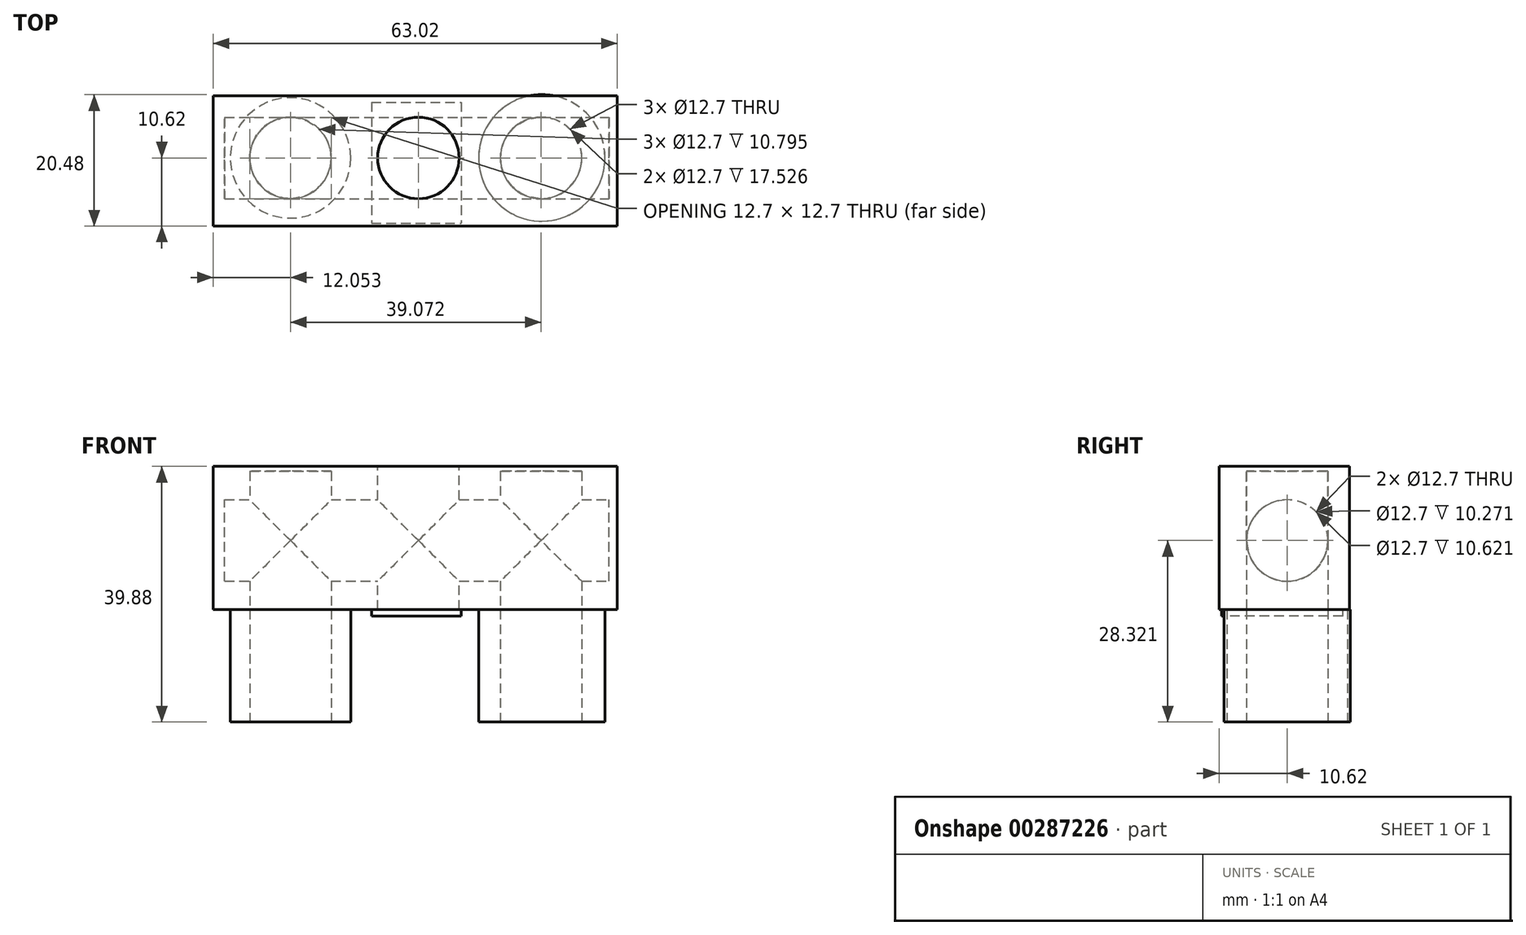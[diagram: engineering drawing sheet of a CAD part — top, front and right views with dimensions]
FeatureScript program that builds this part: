
annotation { "Feature Type Name" : "Feature", "Feature Type Description" : "" }
export const myFeature = defineFeature(function(context is Context, id is Id, definition is map)
    precondition{}
    {
        {
            var Q0;
            Q0=qCreatedBy(makeId("Top.planeOp"),FACE);
            var sketch = newSketch(context, id + "F0", { "sketchPlane" : qUnion([Q0])});
            skCircle(sketch, "E0", {"center": v(-19.95, 0) * mm, "radius": 9.39 * mm});
            skCircle(sketch, "E1", {"center": v(19.24, 0) * mm, "radius": 9.86 * mm});
            skSolve(sketch);
        }
        {
            var Q0;
            Q0 = qSketchRegion(id + "F0", true);
            extrude(context, id + "F1", {"entities" : qUnion([Q0]), "depth" : 17.53 * mm});
        }
        {
            var Q0;
            Q0=makeQuery(id+"F1.opExtrude","CAP_FACE",FACE,{"disambiguationData":[OSD([sQuery(id+"F0.wireOp",EDGE,"E0")])],"isStart":false});
            var sketch = newSketch(context, id + "F2", { "sketchPlane" : qUnion([Q0])});
            skLineSegment(sketch, "E2.bottom", {"start": v(-30.22, 9.68) * mm, "end": v(29.75, 9.68) * mm});
            skLineSegment(sketch, "E2.top", {"start": v(-30.22, -10.62) * mm, "end": v(29.75, -10.62) * mm});
            skLineSegment(sketch, "E2.left", {"start": v(-30.22, 9.68) * mm, "end": v(-30.22, -10.62) * mm});
            skLineSegment(sketch, "E2.right", {"start": v(29.75, 9.68) * mm, "end": v(29.75, -10.62) * mm});
            skSolve(sketch);
        }
        {
            var Q0;
            Q0 = qSketchRegion(id + "F2", true);
            extrude(context, id + "F3", {"entities" : qUnion([Q0]), "depth" : 21.59 * mm});
        }
        {
            var Q0;
            Q0=makeQuery(id+"F3.opExtrude","SWEPT_FACE",FACE,{"disambiguationData":[OSD([sQuery(id+"F2.wireOp",EDGE,"E2.right")])]});
            var sketch = newSketch(context, id + "F4", { "sketchPlane" : qUnion([Q0])});
            skPoint(sketch, "E3", {"position": v(0, 28.32) * mm});
            skPoint(sketch, "E3.positionSnap0", {"position": v(9.68, 28.32) * mm});
            skSolve(sketch);
        }
        {
            var Q0;
            Q0=sQuery(id+"F4.wireOp",VERTEX,"E3");
            var Q1;
            Q1=makeQuery(id+"F3.opExtrude","SWEPT_BODY",BODY,{"disambiguationData":[OSD([sQuery(id+"F2.wireOp",EDGE,"E2.bottom"),sQuery(id+"F2.wireOp",EDGE,"E2.top"),sQuery(id+"F2.wireOp",EDGE,"E2.left"),sQuery(id+"F2.wireOp",EDGE,"E2.right")])]});
            hole(context, id + "F5", {"style" : HoleStyle.SIMPLE, "endStyle" : HoleEndStyle.THROUGH, "holeDiameter" : 12.7 * mm, "tappedDepth" : 12.7 * mm, "tapClearance" : 3, "locations" : qUnion([Q0]), "scope" : qUnion([Q1])});
        }
        {
            var Q0;
            Q0=makeQuery(id+"F1.opExtrude","CAP_FACE",FACE,{"disambiguationData":[OSD([sQuery(id+"F0.wireOp",EDGE,"E0")])],"isStart":true});
            var sketch = newSketch(context, id + "F6", { "sketchPlane" : qUnion([Q0])});
            skPoint(sketch, "E4", {"position": v(-19.95, 0) * mm});
            skPoint(sketch, "E5", {"position": v(19.12, 0) * mm});
            skSolve(sketch);
        }
        {
            var Q0;
            Q0=sQuery(id+"F6.wireOp",VERTEX,"E4");
            var Q1;
            Q1=sQuery(id+"F6.wireOp",VERTEX,"E5");
            var Q2;
            Q2=makeQuery(id+"F3.opExtrude","SWEPT_BODY",BODY,{"disambiguationData":[OSD([sQuery(id+"F2.wireOp",EDGE,"E2.bottom"),sQuery(id+"F2.wireOp",EDGE,"E2.top"),sQuery(id+"F2.wireOp",EDGE,"E2.left"),sQuery(id+"F2.wireOp",EDGE,"E2.right")])]});
            var Q3;
            Q3=makeQuery(id+"F1.opExtrude","SWEPT_BODY",BODY,{"disambiguationData":[OSD([sQuery(id+"F0.wireOp",EDGE,"E0")])]});
            var Q4;
            Q4=makeQuery(id+"F1.opExtrude","SWEPT_BODY",BODY,{"disambiguationData":[OSD([sQuery(id+"F0.wireOp",EDGE,"E1")])]});
            hole(context, id + "F7", {"style" : HoleStyle.SIMPLE, "endStyle" : HoleEndStyle.THROUGH, "holeDiameter" : 12.7 * mm, "tappedDepth" : 12.7 * mm, "tapClearance" : 3, "locations" : qUnion([Q0, Q1]), "scope" : qUnion([Q2, Q3, Q4])});
        }
        {
            var Q0;
            Q0=makeQuery(id+"F3.opExtrude","CAP_FACE",FACE,{"disambiguationData":[OSD([sQuery(id+"F2.wireOp",EDGE,"E2.bottom"),sQuery(id+"F2.wireOp",EDGE,"E2.top"),sQuery(id+"F2.wireOp",EDGE,"E2.left"),sQuery(id+"F2.wireOp",EDGE,"E2.right")])],"isStart":false});
            var sketch = newSketch(context, id + "F8", { "sketchPlane" : qUnion([Q0])});
            skLineSegment(sketch, "E6.bottom", {"start": v(-30.22, -10.62) * mm, "end": v(29.75, -10.62) * mm});
            skLineSegment(sketch, "E6.top", {"start": v(-30.22, 9.68) * mm, "end": v(29.75, 9.68) * mm});
            skLineSegment(sketch, "E6.left", {"start": v(-30.22, -10.62) * mm, "end": v(-30.22, 9.68) * mm});
            skLineSegment(sketch, "E6.right", {"start": v(29.75, -10.62) * mm, "end": v(29.75, 9.68) * mm});
            skSolve(sketch);
        }
        {
            var Q0;
            Q0 = qSketchRegion(id + "F8", true);
            extrude(context, id + "F9", {"entities" : qUnion([Q0]), "operationType" : NewBodyOperationType.ADD, "depth" : 0.76 * mm});
        }
        {
            var Q0;
            Q0=makeQuery(id+"F9.boolean.opBoolean","MERGE",FACE,{"derivedFrom":[makeQuery(id+"F3.opExtrude","SWEPT_FACE",FACE,{"disambiguationData":[OSD([sQuery(id+"F2.wireOp",EDGE,"E2.right")])]}),makeQuery(id+"F9.opExtrude","SWEPT_FACE",FACE,{"disambiguationData":[OSD([sQuery(id+"F8.wireOp",EDGE,"E6.right")])]})]});
            var sketch = newSketch(context, id + "F10", { "sketchPlane" : qUnion([Q0])});
            skLineSegment(sketch, "E7.bottom", {"start": v(-10.62, 17.53) * mm, "end": v(9.68, 17.53) * mm});
            skLineSegment(sketch, "E7.top", {"start": v(-10.62, 39.88) * mm, "end": v(9.68, 39.88) * mm});
            skLineSegment(sketch, "E7.left", {"start": v(-10.62, 17.53) * mm, "end": v(-10.62, 39.88) * mm});
            skLineSegment(sketch, "E7.right", {"start": v(9.68, 17.53) * mm, "end": v(9.68, 39.88) * mm});
            skSolve(sketch);
        }
        {
            var Q0;
            Q0 = qSketchRegion(id + "F10", true);
            extrude(context, id + "F11", {"entities" : qUnion([Q0]), "operationType" : NewBodyOperationType.ADD, "depth" : 1.27 * mm});
        }
        {
            var Q0;
            Q0=makeQuery(id+"F9.boolean.opBoolean","MERGE",FACE,{"derivedFrom":[makeQuery(id+"F3.opExtrude","SWEPT_FACE",FACE,{"disambiguationData":[OSD([sQuery(id+"F2.wireOp",EDGE,"E2.left")])]}),makeQuery(id+"F9.opExtrude","SWEPT_FACE",FACE,{"disambiguationData":[OSD([sQuery(id+"F8.wireOp",EDGE,"E6.left")])]})]});
            var sketch = newSketch(context, id + "F12", { "sketchPlane" : qUnion([Q0])});
            skLineSegment(sketch, "E8.bottom", {"start": v(-9.68, 17.53) * mm, "end": v(10.62, 17.53) * mm});
            skLineSegment(sketch, "E8.top", {"start": v(-9.68, 39.88) * mm, "end": v(10.62, 39.88) * mm});
            skLineSegment(sketch, "E8.left", {"start": v(-9.68, 17.53) * mm, "end": v(-9.68, 39.88) * mm});
            skLineSegment(sketch, "E8.right", {"start": v(10.62, 17.53) * mm, "end": v(10.62, 39.88) * mm});
            skSolve(sketch);
        }
        {
            var Q0;
            Q0=makeQuery(id+"F14.boolean.opBoolean","MERGE",FACE,{"derivedFrom":[makeQuery(id+"F11.boolean.opBoolean","MERGE",FACE,{"derivedFrom":[makeQuery(id+"F9.opExtrude","CAP_FACE",FACE,{"disambiguationData":[OSD([sQuery(id+"F8.wireOp",EDGE,"E6.bottom"),sQuery(id+"F8.wireOp",EDGE,"E6.top"),sQuery(id+"F8.wireOp",EDGE,"E6.left"),sQuery(id+"F8.wireOp",EDGE,"E6.right")])],"isStart":false}),makeQuery(id+"F11.opExtrude","SWEPT_FACE",FACE,{"disambiguationData":[OSD([sQuery(id+"F10.wireOp",EDGE,"E7.top")])]})]}),makeQuery(id+"F14.opExtrude","SWEPT_FACE",FACE,{"disambiguationData":[OSD([sQuery(id+"F12.wireOp",EDGE,"E8.top")])]})]});
            var sketch = newSketch(context, id + "F13", { "sketchPlane" : qUnion([Q0])});
            skPoint(sketch, "E9", {"position": v(0, 0) * mm});
            skSolve(sketch);
        }
        {
            var Q0;
            Q0 = qSketchRegion(id + "F12", true);
            extrude(context, id + "F14", {"entities" : qUnion([Q0]), "operationType" : NewBodyOperationType.ADD, "depth" : 1.78 * mm});
        }
        {
            var Q0;
            Q0=sQuery(id+"F13.wireOp",VERTEX,"E9");
            var Q1;
            Q1=makeQuery(id+"F3.opExtrude","SWEPT_BODY",BODY,{"disambiguationData":[OSD([sQuery(id+"F2.wireOp",EDGE,"E2.bottom"),sQuery(id+"F2.wireOp",EDGE,"E2.top"),sQuery(id+"F2.wireOp",EDGE,"E2.left"),sQuery(id+"F2.wireOp",EDGE,"E2.right")])]});
            var Q2;
            Q2=makeQuery(id+"F1.opExtrude","SWEPT_BODY",BODY,{"disambiguationData":[OSD([sQuery(id+"F0.wireOp",EDGE,"E0")])]});
            var Q3;
            Q3=makeQuery(id+"F1.opExtrude","SWEPT_BODY",BODY,{"disambiguationData":[OSD([sQuery(id+"F0.wireOp",EDGE,"E1")])]});
            hole(context, id + "F15", {"style" : HoleStyle.SIMPLE, "endStyle" : HoleEndStyle.THROUGH, "holeDiameter" : 12.7 * mm, "tappedDepth" : 12.7 * mm, "tapClearance" : 3, "locations" : qUnion([Q0]), "scope" : qUnion([Q1, Q2, Q3])});
        }
        {
            var Q0;
            {var subQ0=sQuery(id+"F2.wireOp",EDGE,"E2.right");Q0=makeQuery(id+"F2.imprint","IMPRINT",FACE,{"disambiguationData":[TD([[makeQuery(id+"F2.imprint","IMPRINT",EDGE,{"derivedFrom":subQ0}),-1.0]])]});}
            var sketch = newSketch(context, id + "F16", { "sketchPlane" : qUnion([Q0])});
            skLineSegment(sketch, "E10.bottom", {"start": v(-7.32, 8.69) * mm, "end": v(6.7, 8.69) * mm});
            skLineSegment(sketch, "E10.top", {"start": v(-7.32, -10.21) * mm, "end": v(6.7, -10.21) * mm});
            skLineSegment(sketch, "E10.left", {"start": v(-7.32, 8.69) * mm, "end": v(-7.32, -10.21) * mm});
            skLineSegment(sketch, "E10.right", {"start": v(6.7, 8.69) * mm, "end": v(6.7, -10.21) * mm});
            skSolve(sketch);
        }
        {
            var Q0;
            Q0 = qSketchRegion(id + "F16", true);
            extrude(context, id + "F17", {"entities" : qUnion([Q0]), "operationType" : NewBodyOperationType.ADD, "oppositeDirection" : true, "depth" : 1.02 * mm});
        }
    });
